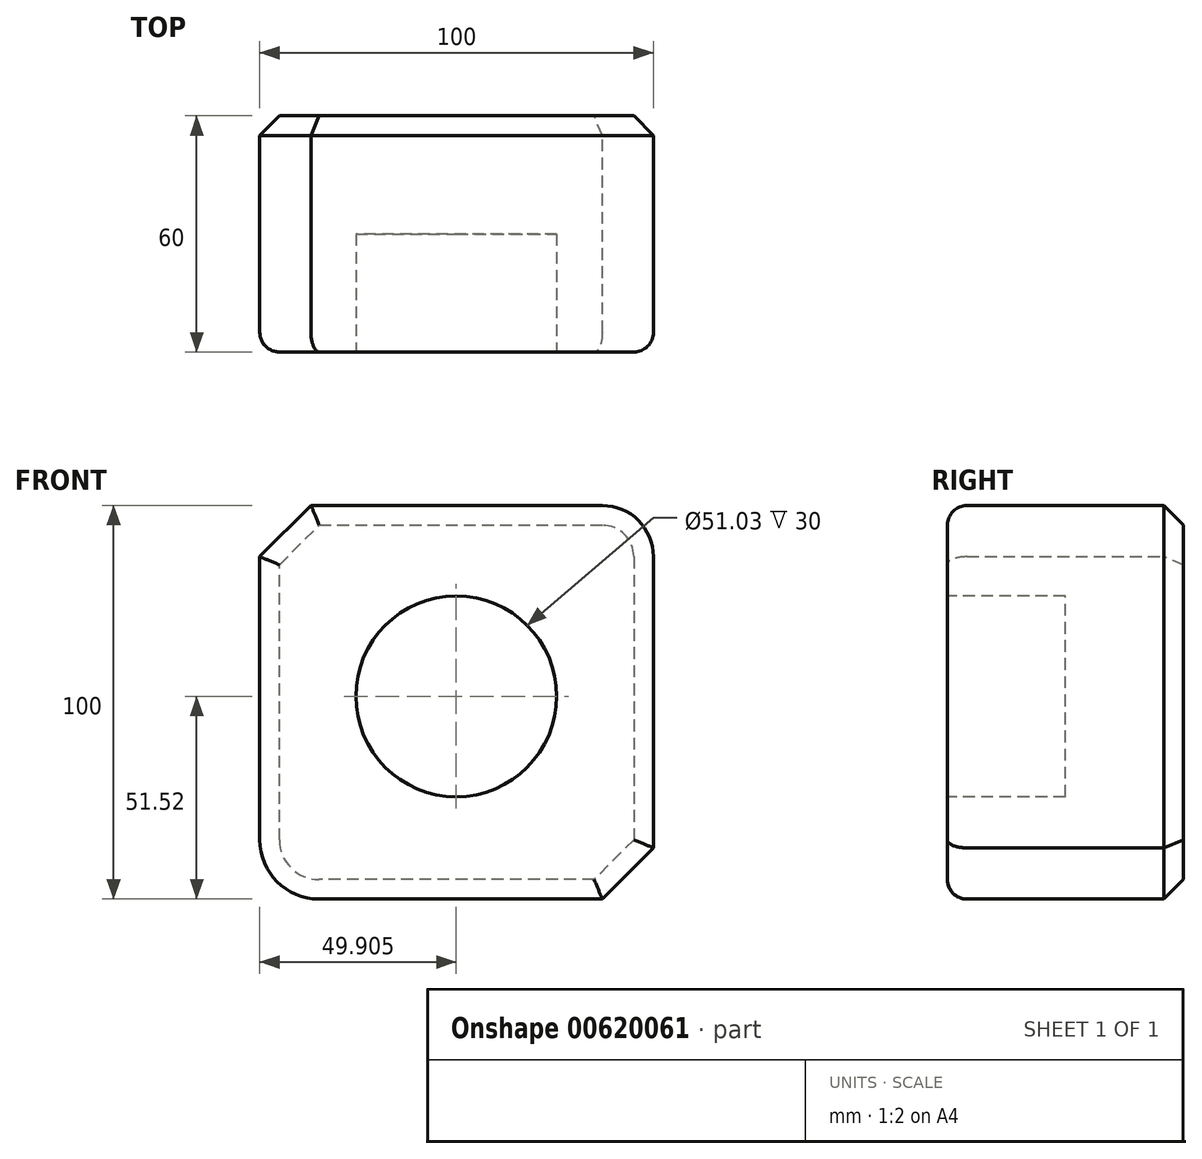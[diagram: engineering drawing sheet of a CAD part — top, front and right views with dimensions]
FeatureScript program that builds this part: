
annotation { "Feature Type Name" : "Feature", "Feature Type Description" : "" }
export const myFeature = defineFeature(function(context is Context, id is Id, definition is map)
    precondition{}
    {
        {
            var Q0;
            Q0=qCreatedBy(makeId("Front.planeOp"),FACE);
            var sketch = newSketch(context, id + "F0", { "sketchPlane" : qUnion([Q0])});
            skLineSegment(sketch, "E0.bottom", {"start": v(-33.94, 48.48) * mm, "end": v(40.06, 48.48) * mm});
            skLineSegment(sketch, "E0.top", {"start": v(-31.94, -51.52) * mm, "end": v(40.06, -51.52) * mm});
            skLineSegment(sketch, "E0.left", {"start": v(-46.94, 35.48) * mm, "end": v(-46.94, -36.52) * mm});
            skLineSegment(sketch, "E0.right", {"start": v(53.06, 35.48) * mm, "end": v(53.06, -38.52) * mm});
            skPoint(sketch, "E1.visualSharp", {"position": v(-46.94, -51.52) * mm});
            skArc(sketch, "E1.filletArc", {"start": v(-46.94, -36.52) * mm, "mid": v(-42.54, -47.13) * mm, "end": v(-31.94, -51.52) * mm});
            skPoint(sketch, "E2.visualSharp", {"position": v(-46.94, 48.48) * mm});
            skPoint(sketch, "E3.visualSharp", {"position": v(53.06, 48.48) * mm});
            skArc(sketch, "E3.filletArc", {"start": v(53.06, 35.48) * mm, "mid": v(49.25, 44.67) * mm, "end": v(40.06, 48.48) * mm});
            skPoint(sketch, "E4.visualSharp", {"position": v(53.06, -51.52) * mm});
            skLineSegment(sketch, "E5", {"start": v(-33.94, 48.48) * mm, "end": v(-46.94, 35.48) * mm});
            skLineSegment(sketch, "E6", {"start": v(53.06, -38.52) * mm, "end": v(40.06, -51.52) * mm});
            skSolve(sketch);
        }
        {
            var Q0;
            Q0=makeQuery(id+"F0.imprint","IMPRINT",FACE,{"disambiguationData":[TD([[makeQuery(id+"F0.imprint","IMPRINT",EDGE,{"derivedFrom":sQuery(id+"F0.wireOp",EDGE,"E0.bottom")}),-1.0]])]});
            extrude(context, id + "F1", {"entities" : qUnion([Q0]), "depth" : 60 * mm, "offsetDistance" : 25 * mm});
        }
        {
            var Q0;
            Q0=makeQuery(id+"F1.opExtrude","CAP_FACE",FACE,{"disambiguationData":[OSD([sQuery(id+"F0.wireOp",EDGE,"E0.bottom"),sQuery(id+"F0.wireOp",EDGE,"E0.top"),sQuery(id+"F0.wireOp",EDGE,"E0.left"),sQuery(id+"F0.wireOp",EDGE,"E0.right"),sQuery(id+"F0.wireOp",EDGE,"E1.filletArc"),sQuery(id+"F0.wireOp",EDGE,"E3.filletArc"),sQuery(id+"F0.wireOp",EDGE,"E5"),sQuery(id+"F0.wireOp",EDGE,"E6")])],"isStart":false});
            fillet(context, id + "F2", {"entities" : qUnion([Q0]), "radius" : 5 * mm, "tangentPropagation" : true, "allowEdgeOverflow" : false});
        }
        {
            var Q0;
            Q0=makeQuery(id+"F1.opExtrude","CAP_FACE",FACE,{"disambiguationData":[OSD([sQuery(id+"F0.wireOp",EDGE,"E0.bottom"),sQuery(id+"F0.wireOp",EDGE,"E0.top"),sQuery(id+"F0.wireOp",EDGE,"E0.left"),sQuery(id+"F0.wireOp",EDGE,"E0.right"),sQuery(id+"F0.wireOp",EDGE,"E1.filletArc"),sQuery(id+"F0.wireOp",EDGE,"E3.filletArc"),sQuery(id+"F0.wireOp",EDGE,"E5"),sQuery(id+"F0.wireOp",EDGE,"E6")])],"isStart":true});
            chamfer(context, id + "F3", {"entities" : qUnion([Q0]), "width" : 5 * mm, "tangentPropagation" : true});
        }
        {
            var Q0;
            Q0=makeQuery(id+"F1.opExtrude","CAP_FACE",FACE,{"disambiguationData":[OSD([sQuery(id+"F0.wireOp",EDGE,"E0.bottom"),sQuery(id+"F0.wireOp",EDGE,"E0.top"),sQuery(id+"F0.wireOp",EDGE,"E0.left"),sQuery(id+"F0.wireOp",EDGE,"E0.right"),sQuery(id+"F0.wireOp",EDGE,"E1.filletArc"),sQuery(id+"F0.wireOp",EDGE,"E3.filletArc"),sQuery(id+"F0.wireOp",EDGE,"E5"),sQuery(id+"F0.wireOp",EDGE,"E6")])],"isStart":false});
            var sketch = newSketch(context, id + "F4", { "sketchPlane" : qUnion([Q0])});
            skCircle(sketch, "E7", {"center": v(2.96, 0) * mm, "radius": 25.52 * mm});
            skSolve(sketch);
        }
        {
            var Q0;
            Q0 = qSketchRegion(id + "F4", true);
            extrude(context, id + "F5", {"entities" : qUnion([Q0]), "operationType" : NewBodyOperationType.REMOVE, "oppositeDirection" : true, "depth" : 30 * mm, "offsetDistance" : 25 * mm});
        }
    });
